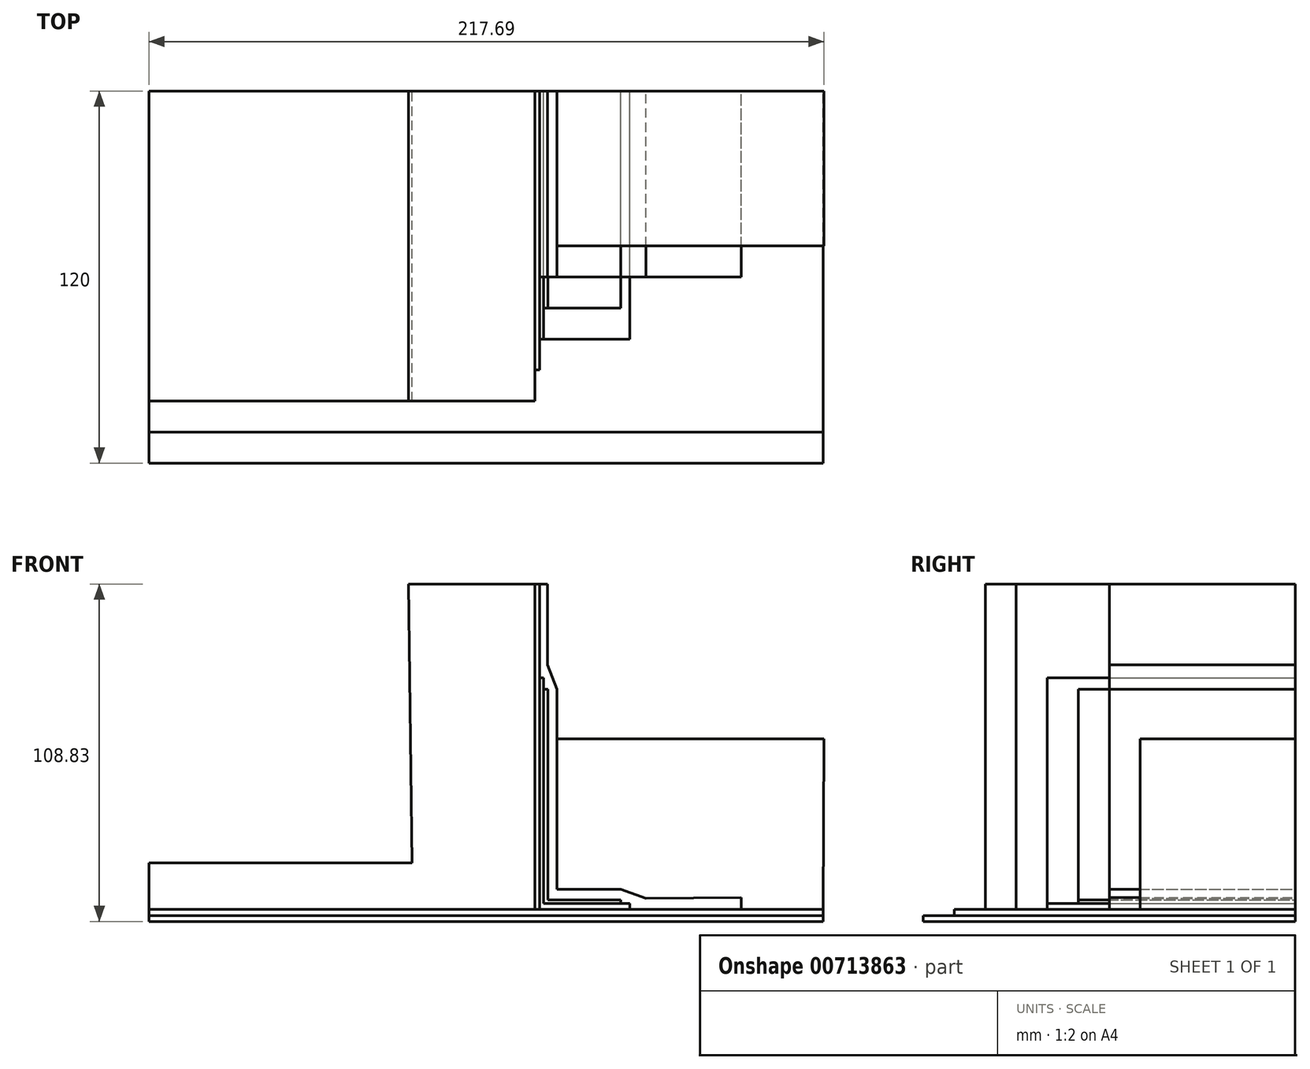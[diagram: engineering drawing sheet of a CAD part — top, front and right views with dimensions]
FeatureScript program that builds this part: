
annotation { "Feature Type Name" : "Feature", "Feature Type Description" : "" }
export const myFeature = defineFeature(function(context is Context, id is Id, definition is map)
    precondition{}
    {
        {
            var Q0;
            Q0=qCreatedBy(makeId("Front.planeOp"),FACE);
            var sketch = newSketch(context, id + "F0", { "sketchPlane" : qUnion([Q0])});
            skLineSegment(sketch, "E0", {"start": v(-68.44, 57.86) * mm, "end": v(-27.72, 57.86) * mm});
            skLineSegment(sketch, "E1", {"start": v(-27.72, 57.86) * mm, "end": v(-27.72, -47.06) * mm});
            skLineSegment(sketch, "E2", {"start": v(-27.72, -47.06) * mm, "end": v(-152.14, -47.06) * mm});
            skLineSegment(sketch, "E3", {"start": v(-152.14, -47.06) * mm, "end": v(-152.14, -32.06) * mm});
            skLineSegment(sketch, "E4", {"start": v(-152.14, -32.06) * mm, "end": v(-67.29, -32.06) * mm});
            skLineSegment(sketch, "E5", {"start": v(-67.29, -32.06) * mm, "end": v(-68.44, 57.86) * mm});
            skLineSegment(sketch, "E6", {"start": v(-152.14, -47.06) * mm, "end": v(-152.14, -49.16) * mm});
            skLineSegment(sketch, "E7", {"start": v(-152.14, -49.16) * mm, "end": v(65.23, -49.16) * mm});
            skLineSegment(sketch, "E8", {"start": v(65.23, -49.16) * mm, "end": v(65.23, -47.06) * mm});
            skLineSegment(sketch, "E9", {"start": v(65.23, -47.06) * mm, "end": v(-27.72, -47.06) * mm});
            skLineSegment(sketch, "E10", {"start": v(-152.14, -49.16) * mm, "end": v(-152.14, -50.97) * mm});
            skLineSegment(sketch, "E11", {"start": v(-152.14, -50.97) * mm, "end": v(65.23, -50.97) * mm});
            skLineSegment(sketch, "E12", {"start": v(65.23, -50.97) * mm, "end": v(65.23, -49.16) * mm});
            skLineSegment(sketch, "E13", {"start": v(-27.72, 57.86) * mm, "end": v(-26.13, 57.86) * mm});
            skLineSegment(sketch, "E14", {"start": v(-26.13, 57.86) * mm, "end": v(-26.13, -47.06) * mm});
            skLineSegment(sketch, "E15", {"start": v(-26.13, 27.62) * mm, "end": v(-24.94, 27.62) * mm});
            skLineSegment(sketch, "E16", {"start": v(-24.94, 27.62) * mm, "end": v(-24.94, -45.23) * mm});
            skLineSegment(sketch, "E17", {"start": v(-24.94, -45.23) * mm, "end": v(2.9, -45.23) * mm});
            skLineSegment(sketch, "E18", {"start": v(2.9, -45.23) * mm, "end": v(2.9, -47.06) * mm});
            skLineSegment(sketch, "E19", {"start": v(-24.94, 23.85) * mm, "end": v(-23.54, 23.85) * mm});
            skLineSegment(sketch, "E20", {"start": v(-23.54, 23.85) * mm, "end": v(-23.54, -43.97) * mm});
            skLineSegment(sketch, "E21", {"start": v(-23.54, -43.97) * mm, "end": v(0, -43.97) * mm});
            skLineSegment(sketch, "E22", {"start": v(0, -43.97) * mm, "end": v(0, -45.23) * mm});
            skLineSegment(sketch, "E23", {"start": v(-26.13, 57.86) * mm, "end": v(-23.6, 57.86) * mm});
            skLineSegment(sketch, "E24", {"start": v(-23.6, 57.86) * mm, "end": v(-23.6, 31.76) * mm});
            skLineSegment(sketch, "E25", {"start": v(-23.6, 31.76) * mm, "end": v(-20.56, 23.96) * mm});
            skLineSegment(sketch, "E26", {"start": v(-20.56, 23.96) * mm, "end": v(-20.56, -40.58) * mm});
            skLineSegment(sketch, "E27", {"start": v(-20.56, -40.58) * mm, "end": v(0, -40.58) * mm});
            skLineSegment(sketch, "E28", {"start": v(0, -40.58) * mm, "end": v(8.14, -43.54) * mm});
            skLineSegment(sketch, "E29", {"start": v(65.23, -47.06) * mm, "end": v(65.23, -47.06) * mm});
            skLineSegment(sketch, "E30", {"start": v(38.9, -43.31) * mm, "end": v(38.9, -47.06) * mm});
            skLineSegment(sketch, "E31", {"start": v(38.9, -47.06) * mm, "end": v(38.92, -46.91) * mm});
            skLineSegment(sketch, "E32", {"start": v(8.14, -43.54) * mm, "end": v(38.9, -43.31) * mm});
            skLineSegment(sketch, "E33", {"start": v(-20.56, 7.95) * mm, "end": v(65.55, 7.95) * mm});
            skLineSegment(sketch, "E34", {"start": v(65.55, 7.95) * mm, "end": v(65.23, -47.06) * mm});
            skSolve(sketch);
        }
        {
            var Q0;
            Q0=makeQuery(id+"F0.imprint","IMPRINT",FACE,{"disambiguationData":[TD([[makeQuery(id+"F0.imprint","IMPRINT",EDGE,{"derivedFrom":sQuery(id+"F0.wireOp",EDGE,"E0")}),-1.0]])]});
            extrude(context, id + "F1", {"entities" : qUnion([Q0]), "depth" : 100 * mm});
        }
        {
            var Q0;
            {var subQ1=sQuery(id+"F0.wireOp",EDGE,"E2");Q0=makeQuery(id+"F0.imprint","IMPRINT",FACE,{"disambiguationData":[TD([[makeQuery(id+"F0.imprint","IMPRINT",EDGE,{"derivedFrom":subQ1}),1.0]])]});}
            extrude(context, id + "F2", {"entities" : qUnion([Q0]), "depth" : 110 * mm});
        }
        {
            var Q0;
            Q0=makeQuery(id+"F0.imprint","IMPRINT",FACE,{"disambiguationData":[TD([[makeQuery(id+"F0.imprint","IMPRINT",EDGE,{"derivedFrom":sQuery(id+"F0.wireOp",EDGE,"E7")}),-1.0]])]});
            extrude(context, id + "F3", {"entities" : qUnion([Q0]), "depth" : 120 * mm});
        }
        {
            var Q0;
            {var subQ4=sQuery(id+"F0.wireOp",EDGE,"E1");Q0=makeQuery(id+"F0.imprint","IMPRINT",FACE,{"disambiguationData":[TD([[makeQuery(id+"F0.imprint","IMPRINT",EDGE,{"derivedFrom":subQ4}),1.0]])]});}
            extrude(context, id + "F4", {"entities" : qUnion([Q0]), "depth" : 90 * mm});
        }
        {
            var Q0;
            {var subQ1=sQuery(id+"F0.wireOp",EDGE,"E15");Q0=makeQuery(id+"F0.imprint","IMPRINT",FACE,{"disambiguationData":[TD([[makeQuery(id+"F0.imprint","IMPRINT",EDGE,{"derivedFrom":subQ1}),-1.0]])]});}
            extrude(context, id + "F5", {"entities" : qUnion([Q0]), "depth" : 80 * mm});
        }
        {
            var Q0;
            {var subQ0=sQuery(id+"F0.wireOp",EDGE,"E19");Q0=makeQuery(id+"F0.imprint","IMPRINT",FACE,{"disambiguationData":[TD([[makeQuery(id+"F0.imprint","IMPRINT",EDGE,{"derivedFrom":subQ0}),-1.0]])]});}
            extrude(context, id + "F6", {"entities" : qUnion([Q0]), "depth" : 70 * mm});
        }
        {
            var Q0;
            {var subQ7=sQuery(id+"F0.wireOp",EDGE,"E15");Q0=makeQuery(id+"F0.imprint","IMPRINT",FACE,{"disambiguationData":[TD([[makeQuery(id+"F0.imprint","IMPRINT",EDGE,{"derivedFrom":subQ7}),1.0]])]});}
            extrude(context, id + "F7", {"entities" : qUnion([Q0]), "depth" : 60 * mm});
        }
        {
            var Q0;
            {var subQ0=sQuery(id+"F0.wireOp",EDGE,"E27");Q0=makeQuery(id+"F0.imprint","IMPRINT",FACE,{"disambiguationData":[TD([[makeQuery(id+"F0.imprint","IMPRINT",EDGE,{"derivedFrom":subQ0}),1.0]])]});}
            extrude(context, id + "F8", {"entities" : qUnion([Q0]), "depth" : 50 * mm});
        }
    });
